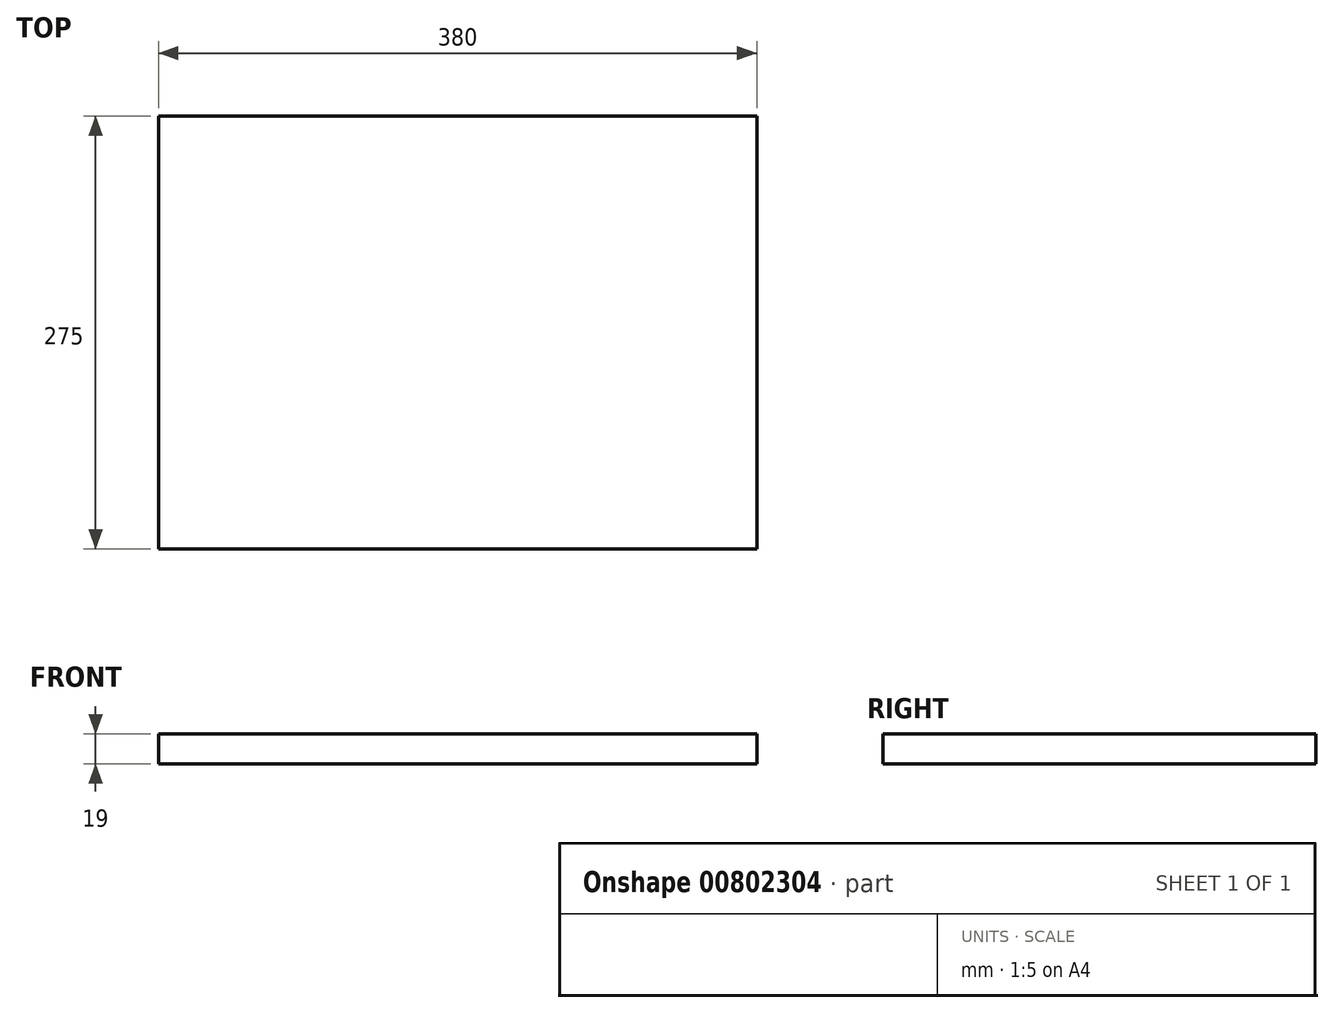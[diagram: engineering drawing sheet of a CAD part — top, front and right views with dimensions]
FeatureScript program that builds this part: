
annotation { "Feature Type Name" : "Feature", "Feature Type Description" : "" }
export const myFeature = defineFeature(function(context is Context, id is Id, definition is map)
    precondition{}
    {
        {
            var Q0;
            Q0=qCreatedBy(makeId("Top.planeOp"),FACE);
            var sketch = newSketch(context, id + "F0", { "sketchPlane" : qUnion([Q0])});
            skLineSegment(sketch, "E0.bottom", {"start": v(-224.35, 197.17) * mm, "end": v(155.65, 197.17) * mm});
            skLineSegment(sketch, "E0.top", {"start": v(-224.35, -77.83) * mm, "end": v(155.65, -77.83) * mm});
            skLineSegment(sketch, "E0.left", {"start": v(-224.35, 197.17) * mm, "end": v(-224.35, -77.83) * mm});
            skLineSegment(sketch, "E0.right", {"start": v(155.65, 197.17) * mm, "end": v(155.65, -77.83) * mm});
            skSolve(sketch);
        }
        {
            var Q0;
            Q0=makeQuery(id+"F0.imprint","IMPRINT",FACE,{"disambiguationData":[TD([[makeQuery(id+"F0.imprint","IMPRINT",EDGE,{"derivedFrom":sQuery(id+"F0.wireOp",EDGE,"E0.bottom")}),-1.0]])]});
            extrude(context, id + "F1", {"entities" : qUnion([Q0]), "depth" : 19 * mm, "offsetDistance" : 25 * mm});
        }
    });
